# Revit family: KB301-01
name_source: partatom
category: Equipement spécialisé
units: mm (PartAtom-declared; Revit-internal decimal feet)

## family parameters
Autoriser la découpe dans les vues = Non
Conserver l'orientation des annotations = Non
Cote de connecteur circulaire = Utiliser le diamètre
Couper avec des vides une fois chargée = Non
Hôte = Face
Numéro OmniClass = 23.40.20.21.37
Partagée = Oui
Repère de localisation dans la pièce = Non
Titre OmniClass = Diaper Changing Units
Type d'élément = Normal

## types (3) — shared parameters
ADA Compliant = Oui
Braille Label = Non
Code d'assemblage = C1030200
Description = Baby Changing Station
Elévation par défaut = 27"
Fabricant = Koala Kare
Finish - Hook = Stainless Steel-Koala Kare-Polished
Height = 35 7/8"
Installation Type = Surface-Mounted
Length = 4"
Microban Antimicrobial Additive = Oui
Price = Prices may vary. Please consult Manufacturer Representative for most up-to-date price list.
Warranty Information = 5-year limited warranty on materials and workmanship and include a provision for replacement caused by vandalism
Width = 20 3/4"

## per-type parameters (varying)
| type | Material | Nom du vendeur / Seller's name | URL |
| KB301-00 | Polypropylene-Koala Kare-Beige | ANOX Diffusion | https://www.anox.fr |
| KB301-01 | Polypropylene-Koala Kare-Grey |  | https://www.koalabear.com |
| KB301-05 | Polypropylene-Koala Kare-White Granite |  | https://www.koalabear.com |

note: column(s) folded — value = type name in every type: Modèle

## geometry (parser evidence)
native form markers: Sweep x2
no freeform markers — native parametric forms only
